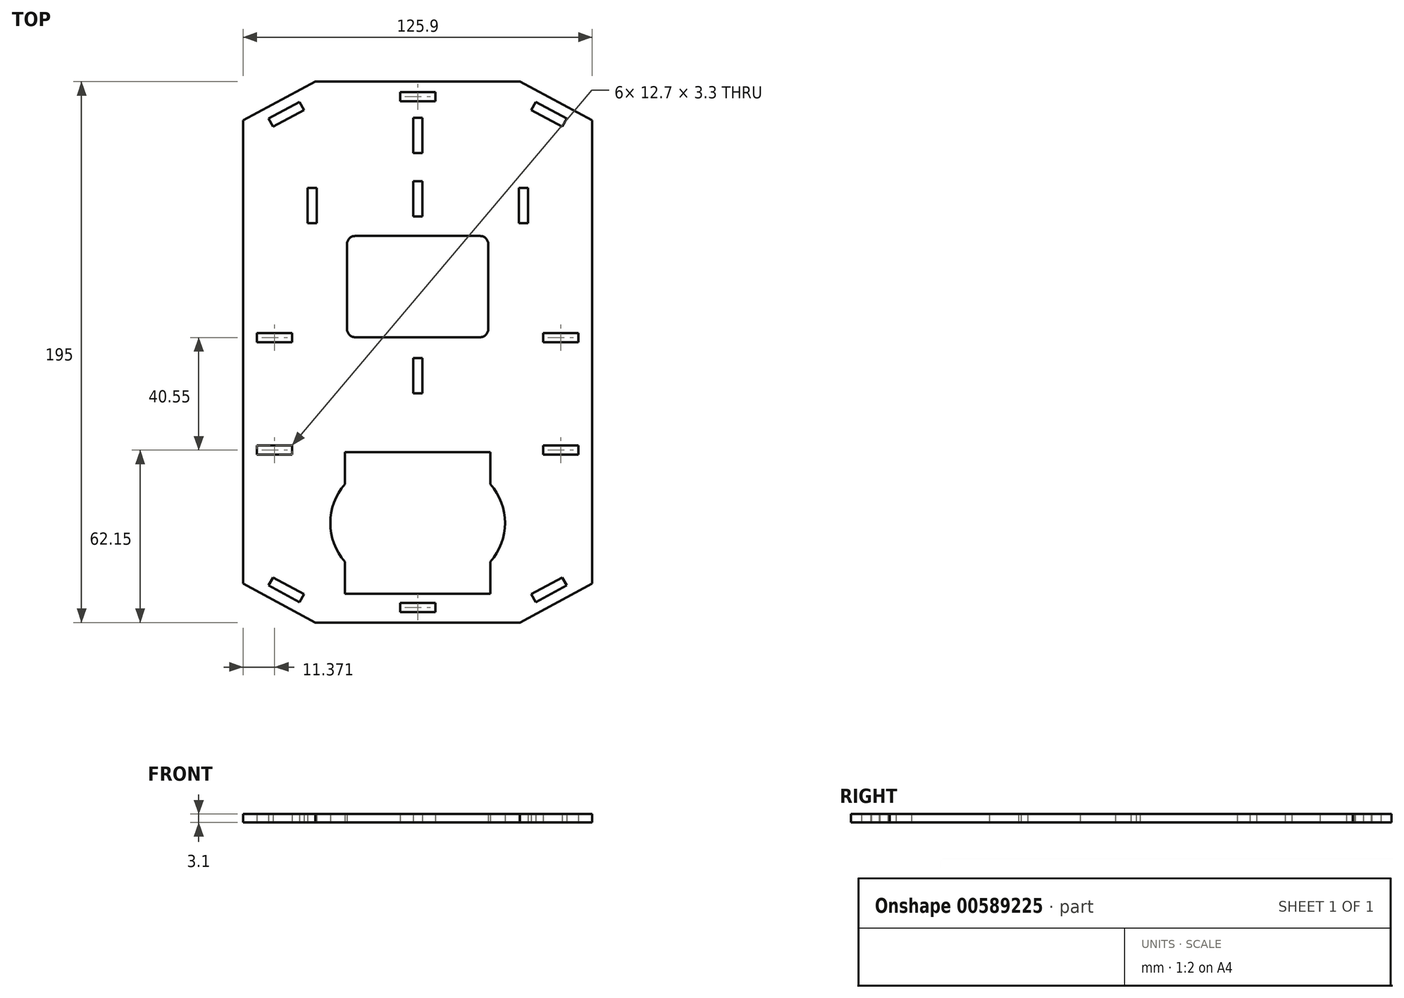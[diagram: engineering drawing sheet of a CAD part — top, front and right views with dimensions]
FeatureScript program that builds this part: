
annotation { "Feature Type Name" : "Feature", "Feature Type Description" : "" }
export const myFeature = defineFeature(function(context is Context, id is Id, definition is map)
    precondition{}
    {
        {
            var Q0;
            Q0=qCreatedBy(makeId("Top.planeOp"),FACE);
            var sketch = newSketch(context, id + "F0", { "sketchPlane" : qUnion([Q0])});
            skLineSegment(sketch, "E0.bottom", {"start": v(-52.17, -81.24) * mm, "end": v(-41, -87.26) * mm});
            skLineSegment(sketch, "E0.top", {"start": v(-53.74, -84.14) * mm, "end": v(-42.56, -90.16) * mm});
            skLineSegment(sketch, "E0.left", {"start": v(-52.17, -81.24) * mm, "end": v(-53.74, -84.14) * mm});
            skLineSegment(sketch, "E0.right", {"start": v(-41, -87.26) * mm, "end": v(-42.56, -90.16) * mm});
            skLineSegment(sketch, "E1", {"start": v(-36.95, -97.5) * mm, "end": v(-62.95, -83.5) * mm});
            skLineSegment(sketch, "E2.bottom", {"start": v(-36.95, -97.5) * mm, "end": v(36.95, -97.5) * mm});
            skLineSegment(sketch, "E2.top", {"start": v(-36.95, 97.5) * mm, "end": v(36.95, 97.5) * mm});
            skLineSegment(sketch, "E2.left", {"start": v(-62.95, -83.5) * mm, "end": v(-62.95, 83.5) * mm});
            skLineSegment(sketch, "E2.right", {"start": v(62.95, -83.5) * mm, "end": v(62.95, 83.5) * mm});
            skLineSegment(sketch, "E3", {"start": v(-48.15, -87.15) * mm, "end": v(-49.95, -90.5) * mm, "construction": true});
            skLineSegment(sketch, "E4.MirrorCS", {"start": v(53.74, -84.14) * mm, "end": v(42.56, -90.16) * mm});
            skLineSegment(sketch, "E5.MirrorCS", {"start": v(52.17, -81.24) * mm, "end": v(53.74, -84.14) * mm});
            skLineSegment(sketch, "E6.MirrorCS", {"start": v(41, -87.26) * mm, "end": v(42.56, -90.16) * mm});
            skLineSegment(sketch, "E7.MirrorCS", {"start": v(52.17, -81.24) * mm, "end": v(41, -87.26) * mm});
            skLineSegment(sketch, "E8.MirrorCS", {"start": v(48.15, -87.15) * mm, "end": v(49.95, -90.5) * mm, "construction": true});
            skLineSegment(sketch, "E9.MirrorCS", {"start": v(36.95, -97.5) * mm, "end": v(62.95, -83.5) * mm});
            skLineSegment(sketch, "E10.MirrorCS", {"start": v(41, 87.26) * mm, "end": v(42.56, 90.16) * mm});
            skLineSegment(sketch, "E11.MirrorCS", {"start": v(52.17, 81.24) * mm, "end": v(53.74, 84.14) * mm});
            skLineSegment(sketch, "E12.MirrorCS", {"start": v(53.74, 84.14) * mm, "end": v(42.56, 90.16) * mm});
            skLineSegment(sketch, "E13.MirrorCS", {"start": v(-41, 87.26) * mm, "end": v(-42.56, 90.16) * mm});
            skLineSegment(sketch, "E14.MirrorCS", {"start": v(-52.17, 81.24) * mm, "end": v(-53.74, 84.14) * mm});
            skLineSegment(sketch, "E15.MirrorCS", {"start": v(-53.74, 84.14) * mm, "end": v(-42.56, 90.16) * mm});
            skLineSegment(sketch, "E16.MirrorCS", {"start": v(-52.17, 81.24) * mm, "end": v(-41, 87.26) * mm});
            skLineSegment(sketch, "E17.MirrorCS", {"start": v(52.17, 81.24) * mm, "end": v(41, 87.26) * mm});
            skLineSegment(sketch, "E18.MirrorCS", {"start": v(48.15, 87.15) * mm, "end": v(49.95, 90.5) * mm, "construction": true});
            skLineSegment(sketch, "E19.MirrorCS", {"start": v(-48.15, 87.15) * mm, "end": v(-49.95, 90.5) * mm, "construction": true});
            skLineSegment(sketch, "E20.MirrorCS", {"start": v(-36.95, 97.5) * mm, "end": v(-62.95, 83.5) * mm});
            skLineSegment(sketch, "E21.MirrorCS", {"start": v(36.95, 97.5) * mm, "end": v(62.95, 83.5) * mm});
            skPoint(sketch, "E22.orphan", {"position": v(-62.95, 97.5) * mm});
            skPoint(sketch, "E23.orphan", {"position": v(62.95, 97.5) * mm});
            skPoint(sketch, "E24.orphan", {"position": v(62.95, -97.5) * mm});
            skPoint(sketch, "E25.orphan", {"position": v(-62.95, -97.5) * mm});
            skLineSegment(sketch, "E26.bottom", {"start": v(-6.35, 90.4) * mm, "end": v(6.35, 90.4) * mm});
            skLineSegment(sketch, "E26.top", {"start": v(-6.35, 93.7) * mm, "end": v(6.35, 93.7) * mm});
            skLineSegment(sketch, "E26.left", {"start": v(-6.35, 90.4) * mm, "end": v(-6.35, 93.7) * mm});
            skLineSegment(sketch, "E26.right", {"start": v(6.35, 90.4) * mm, "end": v(6.35, 93.7) * mm});
            skPoint(sketch, "E26.middle", {"position": v(0, 92.05) * mm});
            skLineSegment(sketch, "E27.bottom", {"start": v(-6.35, -90.4) * mm, "end": v(6.35, -90.4) * mm});
            skLineSegment(sketch, "E27.top", {"start": v(-6.35, -93.7) * mm, "end": v(6.35, -93.7) * mm});
            skLineSegment(sketch, "E27.left", {"start": v(-6.35, -90.4) * mm, "end": v(-6.35, -93.7) * mm});
            skLineSegment(sketch, "E27.right", {"start": v(6.35, -90.4) * mm, "end": v(6.35, -93.7) * mm});
            skLineSegment(sketch, "E28.bottom", {"start": v(-57.93, -33.7) * mm, "end": v(-45.23, -33.7) * mm});
            skLineSegment(sketch, "E28.top", {"start": v(-57.93, -37) * mm, "end": v(-45.23, -37) * mm});
            skLineSegment(sketch, "E28.left", {"start": v(-57.93, -33.7) * mm, "end": v(-57.93, -37) * mm});
            skLineSegment(sketch, "E28.right", {"start": v(-45.23, -33.7) * mm, "end": v(-45.23, -37) * mm});
            skPoint(sketch, "E28.middle", {"position": v(-51.58, -35.35) * mm});
            skLineSegment(sketch, "E29.bottom", {"start": v(-57.93, 6.85) * mm, "end": v(-45.23, 6.85) * mm});
            skLineSegment(sketch, "E29.top", {"start": v(-57.93, 3.55) * mm, "end": v(-45.23, 3.55) * mm});
            skLineSegment(sketch, "E29.left", {"start": v(-57.93, 6.85) * mm, "end": v(-57.93, 3.55) * mm});
            skLineSegment(sketch, "E29.right", {"start": v(-45.23, 6.85) * mm, "end": v(-45.23, 3.55) * mm});
            skPoint(sketch, "E29.middle", {"position": v(-51.58, 5.2) * mm});
            skLineSegment(sketch, "E30.MirrorCS", {"start": v(57.93, 6.85) * mm, "end": v(57.93, 3.55) * mm});
            skLineSegment(sketch, "E31.MirrorCS", {"start": v(45.23, 6.85) * mm, "end": v(45.23, 3.55) * mm});
            skLineSegment(sketch, "E32.MirrorCS", {"start": v(57.93, -33.7) * mm, "end": v(57.93, -37) * mm});
            skLineSegment(sketch, "E33.MirrorCS", {"start": v(45.23, -33.7) * mm, "end": v(45.23, -37) * mm});
            skLineSegment(sketch, "E34.MirrorCS", {"start": v(57.93, 3.55) * mm, "end": v(45.23, 3.55) * mm});
            skLineSegment(sketch, "E35.MirrorCS", {"start": v(57.93, -33.7) * mm, "end": v(45.23, -33.7) * mm});
            skLineSegment(sketch, "E36.MirrorCS", {"start": v(57.93, -37) * mm, "end": v(45.23, -37) * mm});
            skLineSegment(sketch, "E37.MirrorCS", {"start": v(57.93, 6.85) * mm, "end": v(45.23, 6.85) * mm});
            skPoint(sketch, "E38.MirrorP", {"position": v(51.58, -35.35) * mm});
            skPoint(sketch, "E39.MirrorP", {"position": v(51.58, 5.2) * mm});
            skLineSegment(sketch, "E40.bottom", {"start": v(-26.2, -36.1) * mm, "end": v(26.2, -36.1) * mm});
            skLineSegment(sketch, "E40.top", {"start": v(-26.2, -87.1) * mm, "end": v(26.2, -87.1) * mm});
            skLineSegment(sketch, "E40.left", {"start": v(-26.2, -36.1) * mm, "end": v(-26.2, -47.6) * mm});
            skLineSegment(sketch, "E40.right", {"start": v(26.2, -36.1) * mm, "end": v(26.2, -47.6) * mm});
            skPoint(sketch, "E40.middle", {"position": v(0, -61.6) * mm});
            skArc(sketch, "E41", {"start": v(-26.2, -47.6) * mm, "mid": v(-31.5, -61.6) * mm, "end": v(-26.2, -75.6) * mm});
            skArc(sketch, "E42.MirrorCS", {"start": v(26.2, -47.6) * mm, "mid": v(31.5, -61.6) * mm, "end": v(26.2, -75.6) * mm});
            skLineSegment(sketch, "E43.trimOffspring", {"start": v(26.2, -75.6) * mm, "end": v(26.2, -87.1) * mm});
            skLineSegment(sketch, "E44.trimOffspring", {"start": v(-26.2, -75.6) * mm, "end": v(-26.2, -87.1) * mm});
            skLineSegment(sketch, "E45.bottom", {"start": v(-22.5, 5.35) * mm, "end": v(22.5, 5.35) * mm});
            skLineSegment(sketch, "E45.top", {"start": v(-22.5, 41.85) * mm, "end": v(22.5, 41.85) * mm});
            skLineSegment(sketch, "E45.left", {"start": v(-25.5, 8.35) * mm, "end": v(-25.5, 38.85) * mm});
            skLineSegment(sketch, "E45.right", {"start": v(25.5, 8.35) * mm, "end": v(25.5, 38.85) * mm});
            skPoint(sketch, "E45.middle", {"position": v(0, 23.6) * mm});
            skPoint(sketch, "E46.visualSharp", {"position": v(-25.5, 5.35) * mm});
            skArc(sketch, "E46.filletArc", {"start": v(-25.5, 8.35) * mm, "mid": v(-24.62, 6.23) * mm, "end": v(-22.5, 5.35) * mm});
            skPoint(sketch, "E47.visualSharp", {"position": v(-25.5, 41.85) * mm});
            skArc(sketch, "E47.filletArc", {"start": v(-22.5, 41.85) * mm, "mid": v(-24.62, 40.97) * mm, "end": v(-25.5, 38.85) * mm});
            skPoint(sketch, "E48.visualSharp", {"position": v(25.5, 41.85) * mm});
            skArc(sketch, "E48.filletArc", {"start": v(25.5, 38.85) * mm, "mid": v(24.62, 40.97) * mm, "end": v(22.5, 41.85) * mm});
            skPoint(sketch, "E49.visualSharp", {"position": v(25.5, 5.35) * mm});
            skArc(sketch, "E49.filletArc", {"start": v(22.5, 5.35) * mm, "mid": v(24.62, 6.23) * mm, "end": v(25.5, 8.35) * mm});
            skLineSegment(sketch, "E50.bottom", {"start": v(-1.65, 61.55) * mm, "end": v(1.65, 61.55) * mm});
            skLineSegment(sketch, "E50.top", {"start": v(-1.65, 48.85) * mm, "end": v(1.65, 48.85) * mm});
            skLineSegment(sketch, "E50.left", {"start": v(-1.65, 61.55) * mm, "end": v(-1.65, 48.85) * mm});
            skLineSegment(sketch, "E50.right", {"start": v(1.65, 61.55) * mm, "end": v(1.65, 48.85) * mm});
            skPoint(sketch, "E50.middle", {"position": v(0, 55.2) * mm});
            skLineSegment(sketch, "E51.bottom", {"start": v(-1.65, 84.4) * mm, "end": v(1.65, 84.4) * mm});
            skLineSegment(sketch, "E51.top", {"start": v(-1.65, 71.7) * mm, "end": v(1.65, 71.7) * mm});
            skLineSegment(sketch, "E51.left", {"start": v(-1.65, 84.4) * mm, "end": v(-1.65, 71.7) * mm});
            skLineSegment(sketch, "E51.right", {"start": v(1.65, 84.4) * mm, "end": v(1.65, 71.7) * mm});
            skPoint(sketch, "E51.middle", {"position": v(0, 78.05) * mm});
            skPoint(sketch, "E52.MirrorP", {"position": v(0, -9.1) * mm});
            skLineSegment(sketch, "E53.MirrorCS", {"start": v(-1.65, -14.85) * mm, "end": v(-1.65, -2.15) * mm});
            skLineSegment(sketch, "E54.MirrorCS", {"start": v(1.65, -14.85) * mm, "end": v(1.65, -2.15) * mm});
            skLineSegment(sketch, "E55.MirrorCS", {"start": v(-1.65, -14.85) * mm, "end": v(1.65, -14.85) * mm});
            skLineSegment(sketch, "E56.MirrorCS", {"start": v(-1.65, -2.15) * mm, "end": v(1.65, -2.15) * mm});
            skLineSegment(sketch, "E57.bottom", {"start": v(-39.75, 59.15) * mm, "end": v(-36.45, 59.15) * mm});
            skLineSegment(sketch, "E57.top", {"start": v(-39.75, 46.45) * mm, "end": v(-36.45, 46.45) * mm});
            skLineSegment(sketch, "E57.left", {"start": v(-39.75, 59.15) * mm, "end": v(-39.75, 46.45) * mm});
            skLineSegment(sketch, "E57.right", {"start": v(-36.45, 59.15) * mm, "end": v(-36.45, 46.45) * mm});
            skPoint(sketch, "E57.middle", {"position": v(-38.1, 52.8) * mm});
            skLineSegment(sketch, "E58.MirrorCS", {"start": v(39.75, 59.15) * mm, "end": v(36.45, 59.15) * mm});
            skLineSegment(sketch, "E59.MirrorCS", {"start": v(39.75, 46.45) * mm, "end": v(36.45, 46.45) * mm});
            skPoint(sketch, "E60.MirrorP", {"position": v(38.1, 52.8) * mm});
            skLineSegment(sketch, "E61.MirrorCS", {"start": v(36.45, 59.15) * mm, "end": v(36.45, 46.45) * mm});
            skLineSegment(sketch, "E62.MirrorCS", {"start": v(39.75, 59.15) * mm, "end": v(39.75, 46.45) * mm});
            skSolve(sketch);
        }
        {
            var Q0;
            Q0=makeQuery(id+"F0.imprint","IMPRINT",FACE,{"disambiguationData":[TD([[makeQuery(id+"F0.imprint","IMPRINT",EDGE,{"derivedFrom":sQuery(id+"F0.wireOp",EDGE,"E0.bottom")}),1.0]])]});
            extrude(context, id + "F1", {"entities" : qUnion([Q0]), "depth" : 3.1 * mm, "offsetDistance" : 25 * mm});
        }
    });
